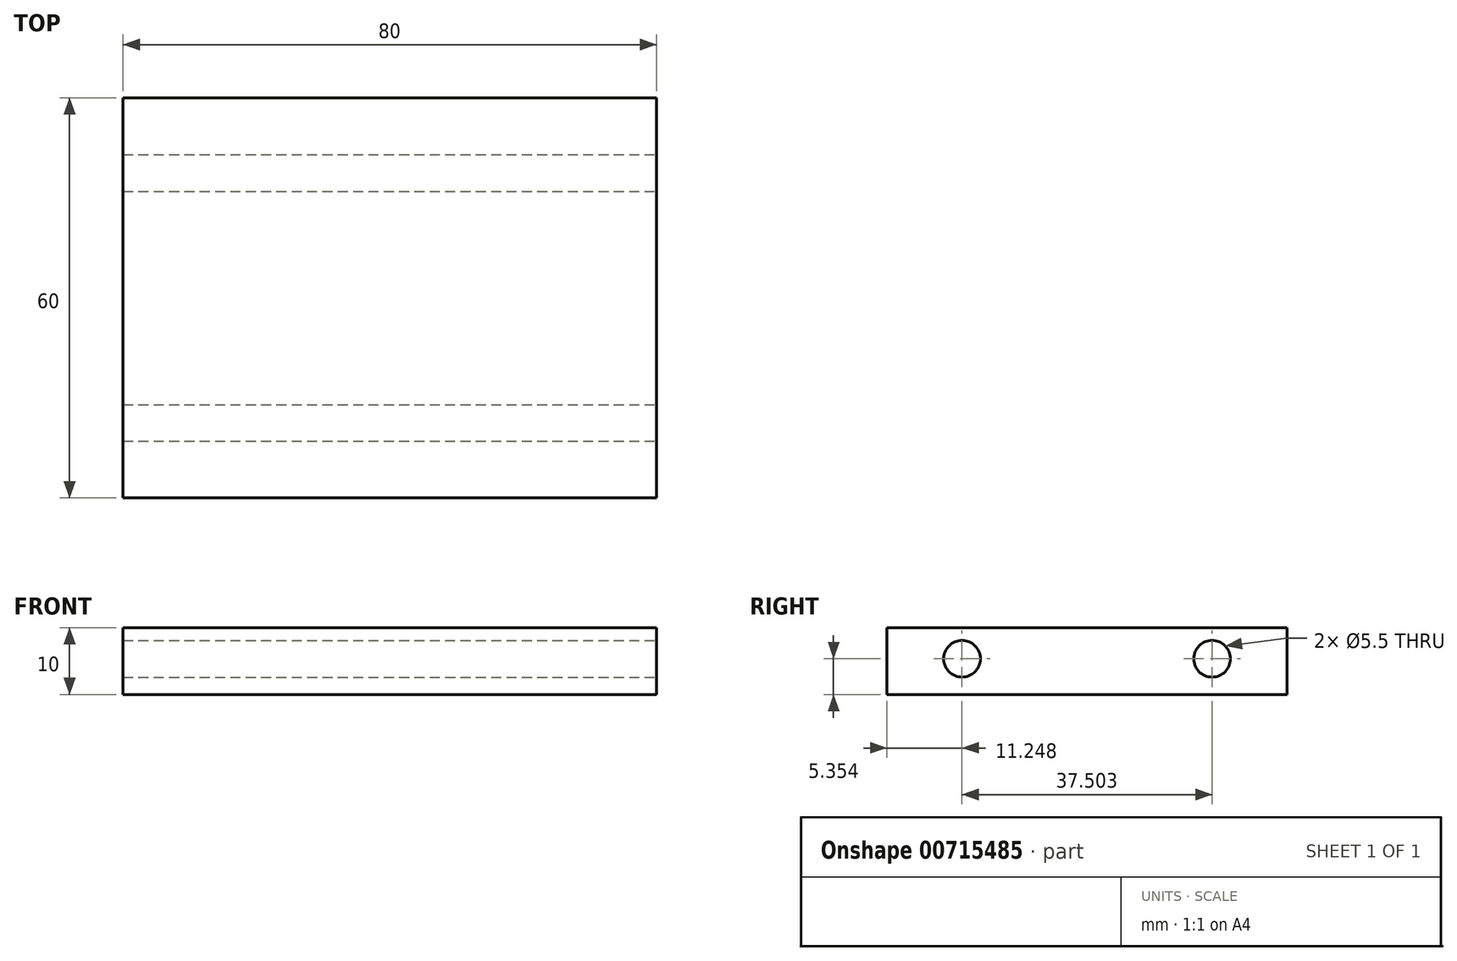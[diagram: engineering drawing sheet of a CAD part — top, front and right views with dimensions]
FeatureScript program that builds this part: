
annotation { "Feature Type Name" : "Feature", "Feature Type Description" : "" }
export const myFeature = defineFeature(function(context is Context, id is Id, definition is map)
    precondition{}
    {
        {
            var Q0;
            Q0=qCreatedBy(makeId("Top.planeOp"),FACE);
            var sketch = newSketch(context, id + "F0", { "sketchPlane" : qUnion([Q0])});
            skLineSegment(sketch, "E0.bottom", {"start": v(40, 30) * mm, "end": v(-40, 30) * mm});
            skLineSegment(sketch, "E0.top", {"start": v(40, -30) * mm, "end": v(-40, -30) * mm});
            skLineSegment(sketch, "E0.left", {"start": v(40, 30) * mm, "end": v(40, -30) * mm});
            skLineSegment(sketch, "E0.right", {"start": v(-40, 30) * mm, "end": v(-40, -30) * mm});
            skPoint(sketch, "E0.middle", {"position": v(0, 0) * mm});
            skSolve(sketch);
        }
        {
            var Q0;
            Q0 = qSketchRegion(id + "F0", true);
            extrude(context, id + "F1", {"entities" : qUnion([Q0]), "flatOperationType" : FlatOperationType.REMOVE, "depth" : 10 * mm, "offsetDistance" : 25.4 * mm, "domain" : OperationDomain.MODEL});
        }
        {
            var Q0;
            Q0=makeQuery(id+"F1.opExtrude","SWEPT_FACE",FACE,{"disambiguationData":[OSD([sQuery(id+"F0.wireOp",EDGE,"E0.left")])]});
            var sketch = newSketch(context, id + "F2", { "sketchPlane" : qUnion([Q0])});
            skCircle(sketch, "E1", {"center": v(-18.75, 5.35) * mm, "radius": 1.5 * mm});
            skCircle(sketch, "E2.MirrorC", {"center": v(18.75, 5.35) * mm, "radius": 1.5 * mm});
            skSolve(sketch);
        }
        {
            var Q0;
            Q0=sQuery(id+"F2.wireOp",VERTEX,"E2.MirrorC.center");
            var Q1;
            Q1=sQuery(id+"F2.wireOp",VERTEX,"E1.center");
            var Q2;
            Q2=makeQuery(id+"F1.opExtrude","SWEPT_BODY",BODY,{"disambiguationData":[OSD([sQuery(id+"F0.wireOp",EDGE,"E0.bottom"),sQuery(id+"F0.wireOp",EDGE,"E0.top"),sQuery(id+"F0.wireOp",EDGE,"E0.left"),sQuery(id+"F0.wireOp",EDGE,"E0.right")])]});
            hole(context, id + "F3", {"style" : HoleStyle.SIMPLE, "endStyle" : HoleEndStyle.THROUGH, "standardTappedOrClearance" : lookupTablePath({ "standard" : "Custom", "fit" : "Normal", "size" : "M5", "type" : "Clearance" }), "standardBlindInLast" : lookupTablePath({ "fit" : "Standard", "standard" : "Custom", "size" : "M5", "type" : "Clearance" }), "holeDiameter" : 5.5 * mm, "majorDiameter" : 6.35 * mm, "isTappedThrough" : true, "tappedDepth" : 12.7 * mm, "tapClearance" : 3, "locations" : qUnion([Q0, Q1]), "scope" : qUnion([Q2])});
        }
    });
